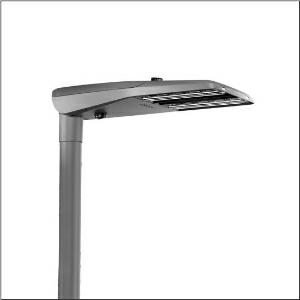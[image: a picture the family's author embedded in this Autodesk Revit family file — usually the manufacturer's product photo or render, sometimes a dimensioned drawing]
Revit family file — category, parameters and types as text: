
# Revit family: streetlight_sl_11_iq_midi___st1_0ab_5xc3n51y08le_be24
name_source: partatom
category: Lighting Fixtures
units: mm (PartAtom-declared; Revit-internal decimal feet)

## family parameters
Cut with Voids When Loaded = No
Host = Face
Light Source = No
Part Type = Normal
Room Calculation Point = No
Round Connector Dimension = Use Diameter
Shared = No

## types (1)
- --- (1 x LED, 7760 lm, 59.4 W, 3000K)
    Apparent Load = 59 VA
    CIE Flux Codes = 29 63 95 100 100
    Color Rendering = 70
    Color Temperature = 3000K
    Default Elevation = 1800 mm
    Description = Streetlight SL 11 iQ midi, mast luminaire, primary light control with 3 zone facetted reflector, of plastic, silver coated, highly specular, primary optical cover: cover, of PMMA, transparent, light distribution: ST1.0aB, light emission: direct distribution, primary light characteristic: asymmetric, installation type: post-top, side-entry, lamps: LED, High Power LED, rated values: 7.760lm | 59,4W | 130,6lm/W (begin service life); end service life: 7.760lm | 61,6W; at 50% lumin. flux: 3.880lm | 28,5W | 136,1lm/W, colour temperature: 3000K, colour rendering: CRI > 70, light colour: 730, light setting 1 begin service life: 100% | 7.760lm | 59,4W | 130,6lm/W | 3.000K, light setting 1 end service life: 61,6W, further light settings possible, control: pre-setting: logarithmic dimming characteristic, Street-Remote, Auto-Match, Temp-Guard, Lumen-Switch, Night-Set, Smart-Wire, Light-Fading, Desk-Remote (wireless, voltage-free reading and setting of iQ features in the workshop via application-optimized NFC function/RFID function), optimised constant luminous flux control (CLO 2.0), with cable H07RN-F 3x 1.5mm², mains connection: 230..240V, AC, 50/60Hz, connection cable pre-assembled, cable length: 8,5m, luminaire housing, of diecast aluminium, powder-coated, SITECO metallic grey (DB 702S), please order mast flange separately, inclination adjustable without tools: 0°, 5°, 10°, 15° (post-top) | 0°, -5°, -10°, -15° (side-entry), sealing non-destructively replaceable, multi-level sealing system, length: 780mm, width: 376mm, height: 118mm, mast flange for spigot size: 42mm (side-entry): 5XC10008XM4, 60/48mm (side-entry/post-top): 5XC10108XM2, 76/60mm (side-entry/post-top): 5XC10108XM1, equipment: standard, Smart Interface below and above, protection rating (complete): IP66, insulation class (complete): insulation class II (safety insulation), certification: CE, ENEC, ENEC+, VDE, UKCA, impact resistance: IK10, permissible operating ambient temperature for outdoor applications: -25..+50°C, standard-compliant lighting for roads and squares, Environmental Product Declaration (EPD) tested and certified by an independent institute, packaging unit: 1 piece

Light Distribution: ST1.0aB
    Height = 118 mm
    Lamp = 1 x LED
    Lamp Light Flux = 7760 lm
    Lamp Power = 59.4 W
    Lamp count = 1
    Length = 780 mm
    Luminous efficacy = 131 lm/W
    Manufacturer = Siteco
    ModVariant = No
    Model = 5XC3N51Y08LE
    Number of Poles = 1
    OnlyDefault = Yes
    Power Factor = 1
    Product Name = Streetlight SL 11 iQ midi | ST1.0aB
    Product group = mast luminaire | pylon top
    ProductGroupID = 6100
    Protection Class = Protection class II
    Protection Degree = IP 66
    RLX_Detail_Level = 1
    RLX_Emergency_Light_Flux = 0 lm
    RLX_Emergency_Type = 0
    RLX_Emergency_Type_DB = No
    RlxData = <blob elided: 69293 chars, md5=6c27b816>
    Socket = socket
    Standby Power = 0 W
    System Light Flux = 7760 lm
    System Power = 59 W
    Type Comments = factory setting: luminous flux: 100 % | dim-lin: 254 | 521 mA
    Type Image = l_1004429.jpg
    URL = http://relux.com
    VarID = @adj_091743
    Voltage = 0 V
    Weight = 0.00 kg
    Width = 376 mm

## geometry (parser evidence)
native form markers: Blend x4, Sweep x11
no freeform markers — native parametric forms only
